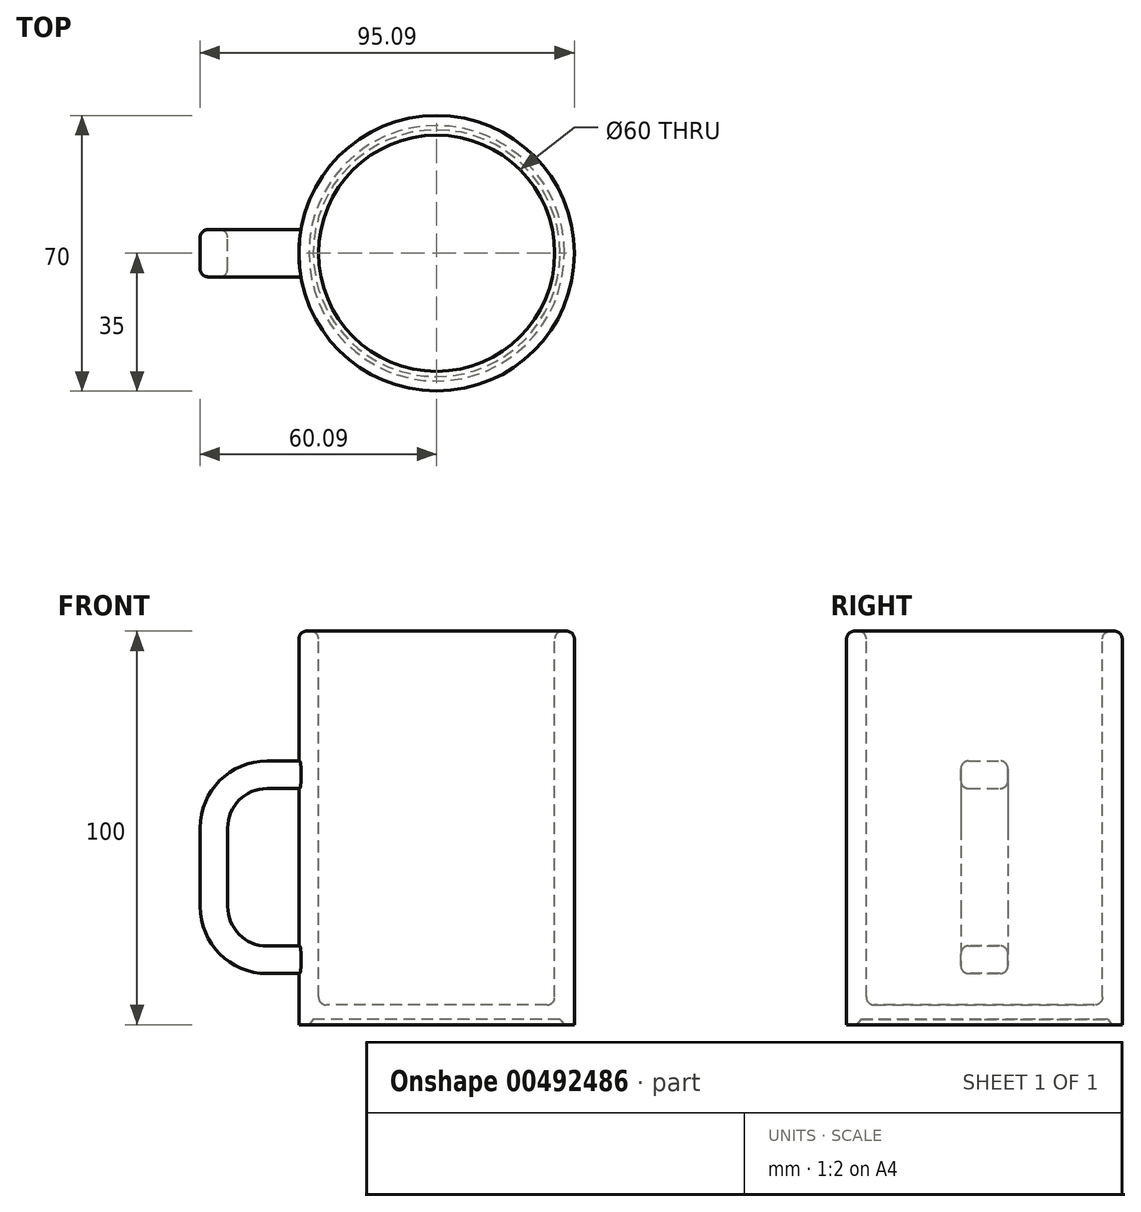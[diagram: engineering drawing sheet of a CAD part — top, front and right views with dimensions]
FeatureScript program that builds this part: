
annotation { "Feature Type Name" : "Feature", "Feature Type Description" : "" }
export const myFeature = defineFeature(function(context is Context, id is Id, definition is map)
    precondition{}
    {
        {
            var Q0;
            Q0=qCreatedBy(makeId("Front.planeOp"),FACE);
            var sketch = newSketch(context, id + "F0", { "sketchPlane" : qUnion([Q0])});
            skLineSegment(sketch, "E0", {"start": v(-137.7, 0) * mm, "end": v(-32.45, 0) * mm, "construction": true});
            skLineSegment(sketch, "E1", {"start": v(0, 127.93) * mm, "end": v(0, 1.38) * mm, "construction": true});
            skLineSegment(sketch, "E2", {"start": v(0, 5) * mm, "end": v(-28, 5) * mm});
            skLineSegment(sketch, "E3", {"start": v(-30, 7) * mm, "end": v(-30, 98) * mm});
            skLineSegment(sketch, "E4", {"start": v(-32, 100) * mm, "end": v(-33, 100) * mm});
            skLineSegment(sketch, "E5", {"start": v(-35, 98) * mm, "end": v(-35, 0) * mm});
            skLineSegment(sketch, "E6", {"start": v(-35, 0) * mm, "end": v(-32.45, 0) * mm});
            skLineSegment(sketch, "E7", {"start": v(0, 5) * mm, "end": v(0, 1.38) * mm});
            skPoint(sketch, "E8.visualSharp", {"position": v(-35, 100) * mm});
            skArc(sketch, "E8.filletArc", {"start": v(-33, 100) * mm, "mid": v(-34.41, 99.41) * mm, "end": v(-35, 98) * mm});
            skPoint(sketch, "E9.visualSharp", {"position": v(-30, 100) * mm});
            skArc(sketch, "E9.filletArc", {"start": v(-30, 98) * mm, "mid": v(-30.59, 99.41) * mm, "end": v(-32, 100) * mm});
            skPoint(sketch, "E10.visualSharp", {"position": v(-30, 5) * mm});
            skArc(sketch, "E10.filletArc", {"start": v(-30, 7) * mm, "mid": v(-29.41, 5.59) * mm, "end": v(-28, 5) * mm});
            skLineSegment(sketch, "E11", {"start": v(-32.45, 0) * mm, "end": v(-31.35, 1.38) * mm});
            skLineSegment(sketch, "E12", {"start": v(-31.35, 1.38) * mm, "end": v(0, 1.38) * mm});
            skLineSegment(sketch, "E13.trimOffspring", {"start": v(0, 0) * mm, "end": v(115.77, 0) * mm, "construction": true});
            skLineSegment(sketch, "E14.trimOffspring", {"start": v(0, 0) * mm, "end": v(0, -104.34) * mm, "construction": true});
            skLineSegment(sketch, "E15", {"start": v(-32.45, 0) * mm, "end": v(0, 0) * mm, "construction": true});
            skSolve(sketch);
        }
        {
            var Q0;
            Q0=makeQuery(id+"F0.imprint","IMPRINT",FACE,{"disambiguationData":[TD([[makeQuery(id+"F0.imprint","IMPRINT",EDGE,{"derivedFrom":sQuery(id+"F0.wireOp",EDGE,"E2")}),1.0]])]});
            var Q1;
            Q1=sQuery(id+"F0.wireOp",EDGE,"E1");
            revolve(context, id + "F1", {"entities" : qUnion([Q0]), "axis" : qUnion([Q1]), "revolveType" : RevolveType.FULL});
        }
        {
            var Q0;
            Q0=qCreatedBy(makeId("Front.planeOp"),FACE);
            var sketch = newSketch(context, id + "F2", { "sketchPlane" : qUnion([Q0])});
            skLineSegment(sketch, "E16", {"start": v(-71.11, 0) * mm, "end": v(51.84, 0) * mm, "construction": true});
            skLineSegment(sketch, "E17", {"start": v(0, 0) * mm, "end": v(0, 89.67) * mm, "construction": true});
            skLineSegment(sketch, "E18", {"start": v(-33.1, 60) * mm, "end": v(-43.1, 60) * mm});
            skLineSegment(sketch, "E19", {"start": v(-53.1, 50) * mm, "end": v(-53.1, 30) * mm});
            skLineSegment(sketch, "E20", {"start": v(-43.1, 20) * mm, "end": v(-33.1, 20) * mm});
            skPoint(sketch, "E21.visualSharp", {"position": v(-53.1, 60) * mm});
            skArc(sketch, "E21.filletArc", {"start": v(-43.1, 60) * mm, "mid": v(-50.16, 57.07) * mm, "end": v(-53.1, 50) * mm});
            skPoint(sketch, "E22.visualSharp", {"position": v(-53.1, 20) * mm});
            skArc(sketch, "E22.filletArc", {"start": v(-53.1, 30) * mm, "mid": v(-50.16, 22.93) * mm, "end": v(-43.1, 20) * mm});
            skLineSegment(sketch, "E23.0", {"start": v(-43.1, 13) * mm, "end": v(-33.1, 13) * mm});
            skLineSegment(sketch, "E23.1", {"start": v(-33.1, 67) * mm, "end": v(-43.1, 67) * mm});
            skArc(sketch, "E23.2", {"start": v(-43.1, 67) * mm, "mid": v(-55.11, 62.02) * mm, "end": v(-60.1, 50) * mm});
            skLineSegment(sketch, "E23.3", {"start": v(-60.1, 50) * mm, "end": v(-60.1, 30) * mm});
            skArc(sketch, "E23.4", {"start": v(-60.1, 30) * mm, "mid": v(-55.11, 17.98) * mm, "end": v(-43.1, 13) * mm});
            skLineSegment(sketch, "E24", {"start": v(-33.1, 67) * mm, "end": v(-33.1, 60) * mm});
            skLineSegment(sketch, "E25", {"start": v(-33.1, 20) * mm, "end": v(-33.1, 13) * mm});
            skSolve(sketch);
        }
        {
            var Q0;
            Q0 = qSketchRegion(id + "F2", true);
            extrude(context, id + "F3", {"entities" : qUnion([Q0]), "operationType" : NewBodyOperationType.ADD, "endBound" : BoundingType.SYMMETRIC, "depth" : 12 * mm});
        }
        {
            var Q0;
            Q0=makeQuery(id+"F3.opExtrude","CAP_EDGE",EDGE,{"disambiguationData":[OSD([sQuery(id+"F2.wireOp",EDGE,"E23.1")])],"isStart":false});
            var Q1;
            Q1=makeQuery(id+"F3.opExtrude","CAP_EDGE",EDGE,{"disambiguationData":[OSD([sQuery(id+"F2.wireOp",EDGE,"E19")])],"isStart":false});
            var Q2;
            Q2=makeQuery(id+"F3.opExtrude","CAP_EDGE",EDGE,{"disambiguationData":[OSD([sQuery(id+"F2.wireOp",EDGE,"E23.2")])],"isStart":true});
            var Q3;
            Q3=makeQuery(id+"F3.opExtrude","CAP_EDGE",EDGE,{"disambiguationData":[OSD([sQuery(id+"F2.wireOp",EDGE,"E19")])],"isStart":true});
            fillet(context, id + "F4", {"entities" : qUnion([Q0, Q1, Q2, Q3]), "radius" : 2 * mm, "tangentPropagation" : true, "allowEdgeOverflow" : false});
        }
    });
